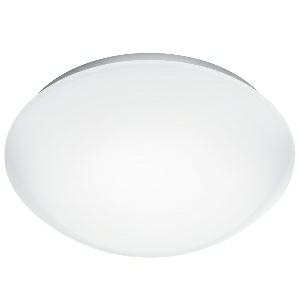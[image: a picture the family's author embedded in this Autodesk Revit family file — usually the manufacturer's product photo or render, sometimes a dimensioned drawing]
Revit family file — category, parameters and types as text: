
# Revit family: rs_pro_led_p3_058609
name_source: partatom
category: Leuchten
revit_build: Autodesk Revit 2016 (Build: 20190508_0715(x64)
units: mm (PartAtom-declared; Revit-internal decimal feet)

## family parameters
Basisbauteil = Fläche
Beim Laden mit Abzugskörper schneiden = Nein
Bemaßung runder Anschluss = Durchmesser verwenden
Gemeinsam genutzt = Nein
Lichtquelle = Nein
Raumberechnungspunkt = Nein
Teiletyp = Normal

## types (1)
- RS PRO LED P3 (1 x , 2210 lm, 3000 K)
    Beschreibung = Dimensions (Ø x H): 400 x 142 mm; Mains power supply: 220 – 240 V / 50 – 60 Hz; Sensor Technology: High frequency; Transmitter power: < 1 mW; HF-system: 5,8 GHz; Output: 20 W; Interconnection: Yes; Type of interconnection: Master/master; Luminous flux: 2210 lm; Luminous flux, emergency light: 38 lm; Colour temperature: 3000 K; Colour variation LED: SDCM3; Colour Rendering Index CRI: 80-89; With lamp: Yes, STEINEL LED system; Lamp: LED cannot be replaced; LED life expectancy (max. °C): 50000 h; Drop in luminous flux in accordance with LM80: L80B10; Base: without; LED cooling system: Passive Thermo Control; With motion detector: Yes; Detection: also through glass, wood and stud walls; Detection angle: 360 °; Angle of aperture: 160 °; Capability of masking out individual segments: Yes; Electronic scalability: Yes; Mechanical scalability: No; Reach, radial: Ø 8 m (50 m²); Reach, tangential: Ø 8 m (50 m²); Continuous light: selectable, 4h; Photo-cell controller: Yes; Twilight setting: 2 – 2000 lx; Time setting: 5 sec – 15 min; Basic light level function: Yes; Basic light level function time: 10/30 min, all night; Soft light start: Yes; Impact resistance: IK03; IP-rating: IP54; Protection class: II; Ambient temperature: 10 – 40 °C; Housing material: Plastic; Cover material: Plastic, opal; Manufacturer's Warranty: 5 years; Settings via: Potentiometers; With remote control: No; Version: Emergency light - warm white; PU1, EAN: 4007841058609
    Color Rendering = 80-89
    Color Temperature = 3000 K
    Frequency = 60 Hz, 50 Hz
    Height = 0 mm  [stored 0 ft]
    Hersteller = Steinel
    Lamp Light Flux = 2210 lm
    Lamp count = 1
    Lampe = 1 x
    Length = 400 mm
    Luminous efficacy = 0 lm/W
    ModVariant = Nein
    Modell = 058609
    Mounting Type = Surface mounted
    Number of Poles = 1
    OnlyDefault = Ja
    Power Factor = 1
    Product Name = RS PRO LED P3
    Product group = Sensor-switched indoor light
    ProductGroupID = 30
    Protection Class = Protection class II
    Protection Degree = IP 54
    RlxData = <blob elided: 34277 chars, md5=eb036540>
    Scheinlast = 20 VA
    Socket = socket
    Standby Power = 0 W
    System Light Flux = 0 lm
    System Power = 20 W
    Typenbild = produkt1_058609.jpg
    Typenkommentare = Product without accessories
    URL = http://relux.com
    VarID = ---
    Voltage = 0 V
    Vorgabe-Ansicht = 1800 mm
    Weight = 0.00 kg
    Width = 0 mm  [stored 0 ft]

note: [stored X ft] marks values corroborated as IEEE doubles in the binary element streams (Revit-internal decimal feet)

## geometry (parser evidence)
native form markers: Blend x4, Sweep x12
no freeform markers — native parametric forms only
